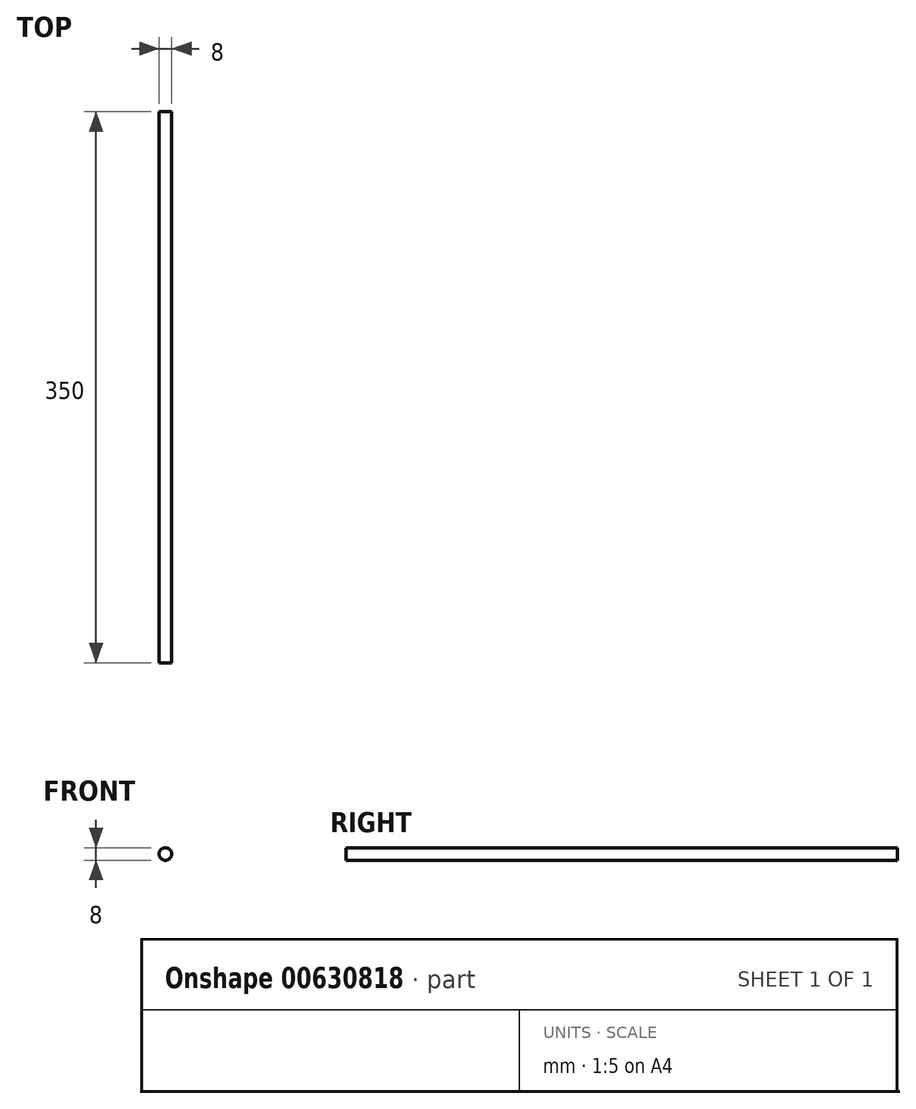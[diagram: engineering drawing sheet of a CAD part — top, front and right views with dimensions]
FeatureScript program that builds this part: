
annotation { "Feature Type Name" : "Feature", "Feature Type Description" : "" }
export const myFeature = defineFeature(function(context is Context, id is Id, definition is map)
    precondition{}
    {
        {
            var Q0;
            Q0=qCreatedBy(makeId("Front.planeOp"),FACE);
            var sketch = newSketch(context, id + "F0", { "sketchPlane" : qUnion([Q0])});
            skCircle(sketch, "E0", {"center": v(0, 0) * mm, "radius": 4 * mm});
            skSolve(sketch);
        }
        {
            var Q0;
            Q0=makeQuery(id+"F0.imprint","IMPRINT",FACE,{"disambiguationData":[TD([[makeQuery(id+"F0.imprint","IMPRINT",EDGE,{"derivedFrom":sQuery(id+"F0.wireOp",EDGE,"E0")}),1.0]])]});
            extrude(context, id + "F1", {"entities" : qUnion([Q0]), "depth" : 350 * mm, "offsetDistance" : 25 * mm});
        }
    });
